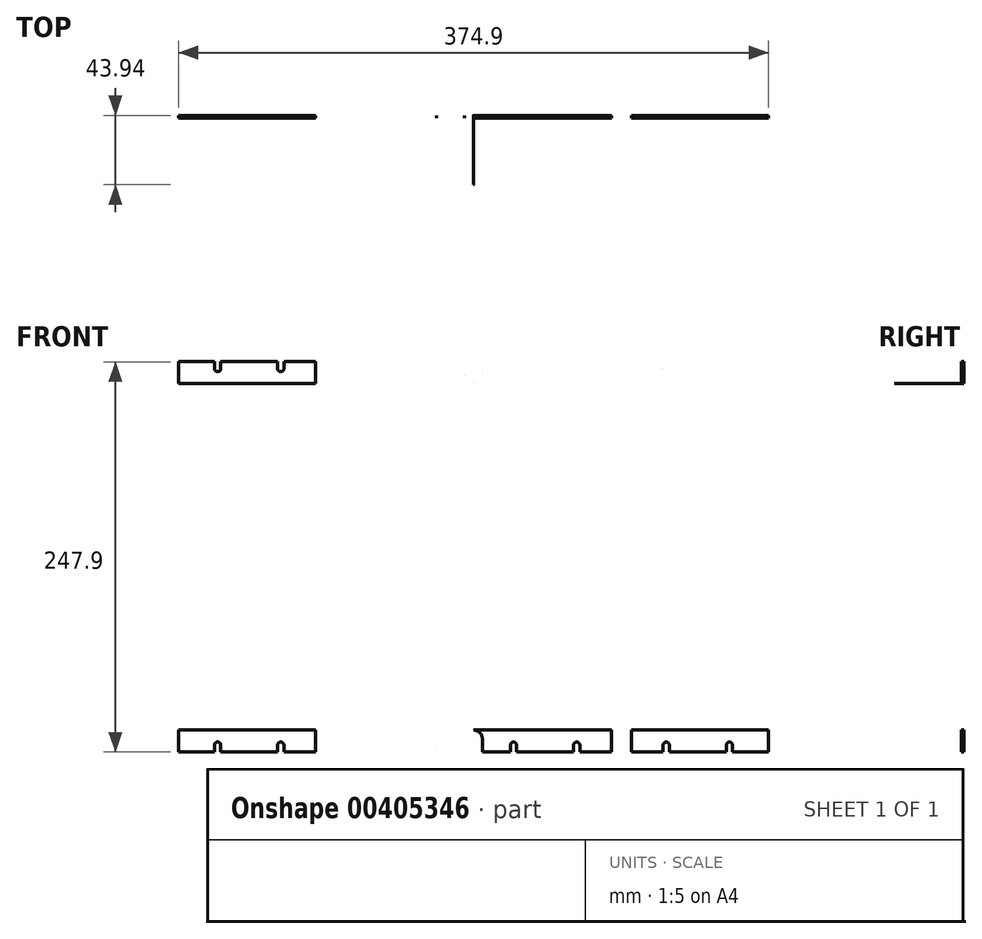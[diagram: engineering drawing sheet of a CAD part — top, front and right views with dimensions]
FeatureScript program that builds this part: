
annotation { "Feature Type Name" : "Feature", "Feature Type Description" : "" }
export const myFeature = defineFeature(function(context is Context, id is Id, definition is map)
    precondition{}
    {
        {
            var Q0;
            Q0=qCreatedBy(makeId("Front.planeOp"),FACE);
            var sketch = newSketch(context, id + "F0", { "sketchPlane" : qUnion([Q0])});
            skLineSegment(sketch, "E0.bottom", {"start": v(-187.45, -123.95) * mm, "end": v(-164.55, -123.95) * mm});
            skLineSegment(sketch, "E0.top", {"start": v(-187.45, 123.95) * mm, "end": v(-164.55, 123.95) * mm});
            skLineSegment(sketch, "E0.left", {"start": v(-187.45, -123.95) * mm, "end": v(-187.45, 123.95) * mm});
            skLineSegment(sketch, "E0.right", {"start": v(187.45, -123.95) * mm, "end": v(187.45, 123.95) * mm});
            skPoint(sketch, "E0.middle", {"position": v(0, 0) * mm});
            skLineSegment(sketch, "E1.0", {"start": v(-187.45, 109.98) * mm, "end": v(187.45, 109.98) * mm});
            skLineSegment(sketch, "E2.0", {"start": v(-187.45, -109.98) * mm, "end": v(187.45, -109.98) * mm});
            skLineSegment(sketch, "E3.0", {"start": v(-187.45, -117.6) * mm, "end": v(187.45, -117.6) * mm, "construction": true});
            skLineSegment(sketch, "E4", {"start": v(0, 123.95) * mm, "end": v(0, 109.98) * mm, "construction": true});
            skLineSegment(sketch, "E5.0", {"start": v(-5.59, 123.95) * mm, "end": v(-5.59, 115.5) * mm});
            skLineSegment(sketch, "E6.0", {"start": v(5.59, 123.95) * mm, "end": v(5.59, 115.5) * mm});
            skLineSegment(sketch, "E7", {"start": v(-187.45, 109.98) * mm, "end": v(-187.45, 123.95) * mm, "construction": true});
            skLineSegment(sketch, "E8.0", {"start": v(-162.56, 109.98) * mm, "end": v(-162.56, 123.95) * mm, "construction": true});
            skLineSegment(sketch, "E9.0", {"start": v(-122.43, 109.98) * mm, "end": v(-122.43, 123.95) * mm, "construction": true});
            skLineSegment(sketch, "E10.0", {"start": v(-65.53, 109.98) * mm, "end": v(-65.53, 123.95) * mm, "construction": true});
            skLineSegment(sketch, "E11.0", {"start": v(-25.4, 109.98) * mm, "end": v(-25.4, 123.95) * mm, "construction": true});
            skLineSegment(sketch, "E12.0", {"start": v(-160.57, 119.58) * mm, "end": v(-160.57, 123.95) * mm});
            skLineSegment(sketch, "E13.0", {"start": v(-164.55, 119.58) * mm, "end": v(-164.55, 123.95) * mm});
            skLineSegment(sketch, "E14", {"start": v(-162.58, 117.6) * mm, "end": v(-162.54, 117.6) * mm});
            skArc(sketch, "E15", {"start": v(-164.55, 119.58) * mm, "mid": v(-162.54, 117.6) * mm, "end": v(-160.57, 119.61) * mm});
            skLineSegment(sketch, "E16.trimOffspring", {"start": v(-160.57, 123.95) * mm, "end": v(-124.42, 123.95) * mm});
            skLineSegment(sketch, "E17.1.0.0", {"start": v(-120.43, 119.58) * mm, "end": v(-120.43, 123.95) * mm});
            skArc(sketch, "E17.1.0.1", {"start": v(-124.42, 119.58) * mm, "mid": v(-122.41, 117.6) * mm, "end": v(-120.43, 119.61) * mm});
            skLineSegment(sketch, "E17.1.0.2", {"start": v(-124.42, 119.58) * mm, "end": v(-124.42, 123.95) * mm});
            skLineSegment(sketch, "E17.direction1", {"start": v(-160.57, 119.58) * mm, "end": v(-120.43, 119.58) * mm, "construction": true});
            skLineSegment(sketch, "E18.trimOffspring", {"start": v(-120.43, 123.95) * mm, "end": v(-100.33, 123.95) * mm});
            skLineSegment(sketch, "E19.1.0.0", {"start": v(-67.53, 119.58) * mm, "end": v(-67.53, 123.95) * mm});
            skArc(sketch, "E19.1.0.1", {"start": v(-67.53, 119.58) * mm, "mid": v(-65.52, 117.6) * mm, "end": v(-63.54, 119.61) * mm});
            skLineSegment(sketch, "E19.1.0.2", {"start": v(-63.54, 119.58) * mm, "end": v(-63.54, 123.95) * mm});
            skLineSegment(sketch, "E19.1.0.3", {"start": v(-27.4, 119.58) * mm, "end": v(-27.4, 123.95) * mm});
            skArc(sketch, "E19.1.0.4", {"start": v(-27.4, 119.58) * mm, "mid": v(-25.38, 117.6) * mm, "end": v(-23.4, 119.61) * mm});
            skLineSegment(sketch, "E19.1.0.5", {"start": v(-23.4, 119.58) * mm, "end": v(-23.4, 123.95) * mm});
            skLineSegment(sketch, "E19.direction1", {"start": v(-164.55, 119.58) * mm, "end": v(-67.53, 119.58) * mm, "construction": true});
            skLineSegment(sketch, "E20.MirrorCS", {"start": v(23.4, 119.58) * mm, "end": v(23.4, 123.95) * mm});
            skArc(sketch, "E21.MirrorCS", {"start": v(27.4, 119.58) * mm, "mid": v(25.38, 117.6) * mm, "end": v(23.4, 119.61) * mm});
            skLineSegment(sketch, "E22.MirrorCS", {"start": v(27.4, 119.58) * mm, "end": v(27.4, 123.95) * mm});
            skLineSegment(sketch, "E23.MirrorCS", {"start": v(63.54, 119.58) * mm, "end": v(63.54, 123.95) * mm});
            skArc(sketch, "E24.MirrorCS", {"start": v(67.53, 119.58) * mm, "mid": v(65.52, 117.6) * mm, "end": v(63.54, 119.61) * mm});
            skLineSegment(sketch, "E25.MirrorCS", {"start": v(67.53, 119.58) * mm, "end": v(67.53, 123.95) * mm});
            skLineSegment(sketch, "E26.MirrorCS", {"start": v(120.43, 119.58) * mm, "end": v(120.43, 123.95) * mm});
            skArc(sketch, "E27.MirrorCS", {"start": v(124.42, 119.58) * mm, "mid": v(122.41, 117.6) * mm, "end": v(120.43, 119.61) * mm});
            skLineSegment(sketch, "E28.MirrorCS", {"start": v(124.42, 119.58) * mm, "end": v(124.42, 123.95) * mm});
            skLineSegment(sketch, "E29.MirrorCS", {"start": v(160.57, 119.58) * mm, "end": v(160.57, 123.95) * mm});
            skArc(sketch, "E30.MirrorCS", {"start": v(164.55, 119.58) * mm, "mid": v(162.54, 117.6) * mm, "end": v(160.57, 119.61) * mm});
            skLineSegment(sketch, "E31.MirrorCS", {"start": v(164.55, 119.58) * mm, "end": v(164.55, 123.95) * mm});
            skLineSegment(sketch, "E32.trimOffspring", {"start": v(164.55, 123.95) * mm, "end": v(187.45, 123.95) * mm});
            skLineSegment(sketch, "E33.trimOffspring", {"start": v(124.42, 123.95) * mm, "end": v(160.57, 123.95) * mm});
            skLineSegment(sketch, "E34.trimOffspring", {"start": v(67.53, 123.95) * mm, "end": v(87.63, 123.95) * mm});
            skLineSegment(sketch, "E35.trimOffspring", {"start": v(27.4, 123.95) * mm, "end": v(63.54, 123.95) * mm});
            skLineSegment(sketch, "E36.trimOffspring", {"start": v(-63.54, 123.95) * mm, "end": v(-27.4, 123.95) * mm});
            skLineSegment(sketch, "E37.trimOffspring", {"start": v(-23.4, 123.95) * mm, "end": v(-5.59, 123.95) * mm});
            skLineSegment(sketch, "E38.MirrorCS", {"start": v(164.55, -119.58) * mm, "end": v(164.55, -123.95) * mm});
            skArc(sketch, "E39.MirrorCS", {"start": v(164.55, -119.58) * mm, "mid": v(162.54, -117.6) * mm, "end": v(160.57, -119.61) * mm});
            skLineSegment(sketch, "E40.MirrorCS", {"start": v(160.57, -119.58) * mm, "end": v(160.57, -123.95) * mm});
            skLineSegment(sketch, "E41.MirrorCS", {"start": v(124.42, -119.58) * mm, "end": v(124.42, -123.95) * mm});
            skArc(sketch, "E42.MirrorCS", {"start": v(124.42, -119.58) * mm, "mid": v(122.41, -117.6) * mm, "end": v(120.43, -119.61) * mm});
            skLineSegment(sketch, "E43.MirrorCS", {"start": v(120.43, -119.58) * mm, "end": v(120.43, -123.95) * mm});
            skLineSegment(sketch, "E44.MirrorCS", {"start": v(67.53, -119.58) * mm, "end": v(67.53, -123.95) * mm});
            skArc(sketch, "E45.MirrorCS", {"start": v(67.53, -119.58) * mm, "mid": v(65.52, -117.6) * mm, "end": v(63.54, -119.61) * mm});
            skLineSegment(sketch, "E46.MirrorCS", {"start": v(63.54, -119.58) * mm, "end": v(63.54, -123.95) * mm});
            skLineSegment(sketch, "E47.MirrorCS", {"start": v(27.4, -119.58) * mm, "end": v(27.4, -123.95) * mm});
            skArc(sketch, "E48.MirrorCS", {"start": v(27.4, -119.58) * mm, "mid": v(25.38, -117.6) * mm, "end": v(23.4, -119.61) * mm});
            skLineSegment(sketch, "E49.MirrorCS", {"start": v(23.4, -119.58) * mm, "end": v(23.4, -123.95) * mm});
            skLineSegment(sketch, "E50.MirrorCS", {"start": v(-23.4, -119.58) * mm, "end": v(-23.4, -123.95) * mm});
            skArc(sketch, "E51.MirrorCS", {"start": v(-27.4, -119.58) * mm, "mid": v(-25.38, -117.6) * mm, "end": v(-23.4, -119.61) * mm});
            skLineSegment(sketch, "E52.MirrorCS", {"start": v(-27.4, -119.58) * mm, "end": v(-27.4, -123.95) * mm});
            skLineSegment(sketch, "E53.MirrorCS", {"start": v(-63.54, -119.58) * mm, "end": v(-63.54, -123.95) * mm});
            skArc(sketch, "E54.MirrorCS", {"start": v(-67.53, -119.58) * mm, "mid": v(-65.52, -117.6) * mm, "end": v(-63.54, -119.61) * mm});
            skLineSegment(sketch, "E55.MirrorCS", {"start": v(-67.53, -119.58) * mm, "end": v(-67.53, -123.95) * mm});
            skLineSegment(sketch, "E56.MirrorCS", {"start": v(-120.43, -119.58) * mm, "end": v(-120.43, -123.95) * mm});
            skArc(sketch, "E57.MirrorCS", {"start": v(-124.42, -119.58) * mm, "mid": v(-122.41, -117.6) * mm, "end": v(-120.43, -119.61) * mm});
            skLineSegment(sketch, "E58.MirrorCS", {"start": v(-124.42, -119.58) * mm, "end": v(-124.42, -123.95) * mm});
            skLineSegment(sketch, "E59.MirrorCS", {"start": v(-160.57, -119.58) * mm, "end": v(-160.57, -123.95) * mm});
            skArc(sketch, "E60.MirrorCS", {"start": v(-164.55, -119.58) * mm, "mid": v(-162.54, -117.6) * mm, "end": v(-160.57, -119.61) * mm});
            skLineSegment(sketch, "E61.MirrorCS", {"start": v(-164.55, -119.58) * mm, "end": v(-164.55, -123.95) * mm});
            skLineSegment(sketch, "E62.trimOffspring", {"start": v(-160.57, -123.95) * mm, "end": v(-124.42, -123.95) * mm});
            skLineSegment(sketch, "E63.trimOffspring", {"start": v(-120.43, -123.95) * mm, "end": v(-100.33, -123.95) * mm});
            skLineSegment(sketch, "E64.trimOffspring", {"start": v(-63.54, -123.95) * mm, "end": v(-27.4, -123.95) * mm});
            skLineSegment(sketch, "E65.trimOffspring", {"start": v(-23.4, -123.95) * mm, "end": v(-5.59, -123.95) * mm});
            skLineSegment(sketch, "E66.trimOffspring", {"start": v(27.4, -123.95) * mm, "end": v(63.54, -123.95) * mm});
            skLineSegment(sketch, "E67.trimOffspring", {"start": v(67.53, -123.95) * mm, "end": v(87.63, -123.95) * mm});
            skLineSegment(sketch, "E68.trimOffspring", {"start": v(124.42, -123.95) * mm, "end": v(160.57, -123.95) * mm});
            skLineSegment(sketch, "E69.trimOffspring", {"start": v(164.55, -123.95) * mm, "end": v(187.45, -123.95) * mm});
            skArc(sketch, "E70", {"start": v(-5.59, 115.63) * mm, "mid": v(0, 109.98) * mm, "end": v(5.59, 115.63) * mm});
            skLineSegment(sketch, "E71.trimOffspring", {"start": v(5.59, 123.95) * mm, "end": v(23.4, 123.95) * mm});
            skLineSegment(sketch, "E72.MirrorCS", {"start": v(5.59, -123.95) * mm, "end": v(5.59, -115.5) * mm});
            skArc(sketch, "E73.MirrorCS", {"start": v(-5.59, -115.63) * mm, "mid": v(0, -109.98) * mm, "end": v(5.59, -115.63) * mm});
            skLineSegment(sketch, "E74.MirrorCS", {"start": v(-5.59, -123.95) * mm, "end": v(-5.59, -115.5) * mm});
            skLineSegment(sketch, "E75.trimOffspring", {"start": v(5.59, -123.95) * mm, "end": v(23.4, -123.95) * mm});
            skLineSegment(sketch, "E76", {"start": v(-93.98, 123.95) * mm, "end": v(-93.98, 109.98) * mm, "construction": true});
            skLineSegment(sketch, "E77.0", {"start": v(-100.33, 123.95) * mm, "end": v(-100.33, 109.98) * mm});
            skLineSegment(sketch, "E78.0", {"start": v(-87.63, 123.95) * mm, "end": v(-87.63, 109.98) * mm});
            skLineSegment(sketch, "E79.MirrorCS", {"start": v(87.63, 123.95) * mm, "end": v(87.63, 109.98) * mm});
            skLineSegment(sketch, "E80.MirrorCS", {"start": v(100.33, 123.95) * mm, "end": v(100.33, 109.98) * mm});
            skLineSegment(sketch, "E81.MirrorCS", {"start": v(100.33, -123.95) * mm, "end": v(100.33, -109.98) * mm});
            skLineSegment(sketch, "E82.MirrorCS", {"start": v(87.63, -123.95) * mm, "end": v(87.63, -109.98) * mm});
            skLineSegment(sketch, "E83.MirrorCS", {"start": v(-87.63, -123.95) * mm, "end": v(-87.63, -109.98) * mm});
            skLineSegment(sketch, "E84.MirrorCS", {"start": v(-100.33, -123.95) * mm, "end": v(-100.33, -109.98) * mm});
            skLineSegment(sketch, "E85.trimOffspring", {"start": v(-87.63, 123.95) * mm, "end": v(-67.53, 123.95) * mm});
            skLineSegment(sketch, "E86.trimOffspring", {"start": v(100.33, 123.95) * mm, "end": v(120.43, 123.95) * mm});
            skLineSegment(sketch, "E87.trimOffspring", {"start": v(100.33, -123.95) * mm, "end": v(120.43, -123.95) * mm});
            skLineSegment(sketch, "E88.trimOffspring", {"start": v(-87.63, -123.95) * mm, "end": v(-67.53, -123.95) * mm});
            skSolve(sketch);
        }
        {
            var Q0;
            {var subQ0=sQuery(id+"F0.wireOp",EDGE,"E1.0");Q0=makeQuery(id+"F0.imprint","IMPRINT",FACE,{"disambiguationData":[TD([[makeQuery(id+"F0.imprint","IMPRINT",EDGE,{"derivedFrom":subQ0}),-1.0]])]});}
            extrude(context, id + "F1", {"entities" : qUnion([Q0]), "depth" : 43.94 * mm});
        }
        {
            var Q0;
            {var subQ0=sQuery(id+"F0.wireOp",EDGE,"E0.top");Q0=makeQuery(id+"F0.imprint","IMPRINT",FACE,{"disambiguationData":[TD([[makeQuery(id+"F0.imprint","IMPRINT",EDGE,{"derivedFrom":subQ0}),-1.0]])]});}
            var Q1;
            {var subQ0=sQuery(id+"F0.wireOp",EDGE,"E0.bottom");Q1=makeQuery(id+"F0.imprint","IMPRINT",FACE,{"disambiguationData":[TD([[makeQuery(id+"F0.imprint","IMPRINT",EDGE,{"derivedFrom":subQ0}),1.0]])]});}
            var Q2;
            {var subQ5=sQuery(id+"F0.wireOp",EDGE,"E6.0");Q2=makeQuery(id+"F0.imprint","IMPRINT",FACE,{"disambiguationData":[TD([[makeQuery(id+"F0.imprint","IMPRINT",EDGE,{"derivedFrom":subQ5}),1.0]])]});}
            var Q3;
            Q3=makeQuery(id+"F0.imprint","IMPRINT",FACE,{"disambiguationData":[TD([[makeQuery(id+"F0.imprint","IMPRINT",EDGE,{"derivedFrom":sQuery(id+"F0.wireOp",EDGE,"E38.MirrorCS")}),1.0]])]});
            var Q4;
            {var subQ10=sQuery(id+"F0.wireOp",EDGE,"E5.0");Q4=makeQuery(id+"F0.imprint","IMPRINT",FACE,{"disambiguationData":[TD([[makeQuery(id+"F0.imprint","IMPRINT",EDGE,{"derivedFrom":subQ10}),-1.0]])]});}
            var Q5;
            {var subQ11=sQuery(id+"F0.wireOp",EDGE,"E50.MirrorCS");Q5=makeQuery(id+"F0.imprint","IMPRINT",FACE,{"disambiguationData":[TD([[makeQuery(id+"F0.imprint","IMPRINT",EDGE,{"derivedFrom":subQ11}),1.0]])]});}
            var Q6;
            Q6=makeQuery(id+"F0.imprint","IMPRINT",FACE,{"disambiguationData":[TD([[makeQuery(id+"F0.imprint","IMPRINT",EDGE,{"derivedFrom":sQuery(id+"F0.wireOp",EDGE,"E44.MirrorCS")}),1.0]])]});
            var Q7;
            {var subQ8=sQuery(id+"F0.wireOp",EDGE,"E26.MirrorCS");Q7=makeQuery(id+"F0.imprint","IMPRINT",FACE,{"disambiguationData":[TD([[makeQuery(id+"F0.imprint","IMPRINT",EDGE,{"derivedFrom":subQ8}),1.0]])]});}
            extrude(context, id + "F2", {"entities" : qUnion([Q0, Q1, Q2, Q3, Q4, Q5, Q6, Q7]), "operationType" : NewBodyOperationType.ADD, "depth" : 1.59 * mm});
        }
    });
